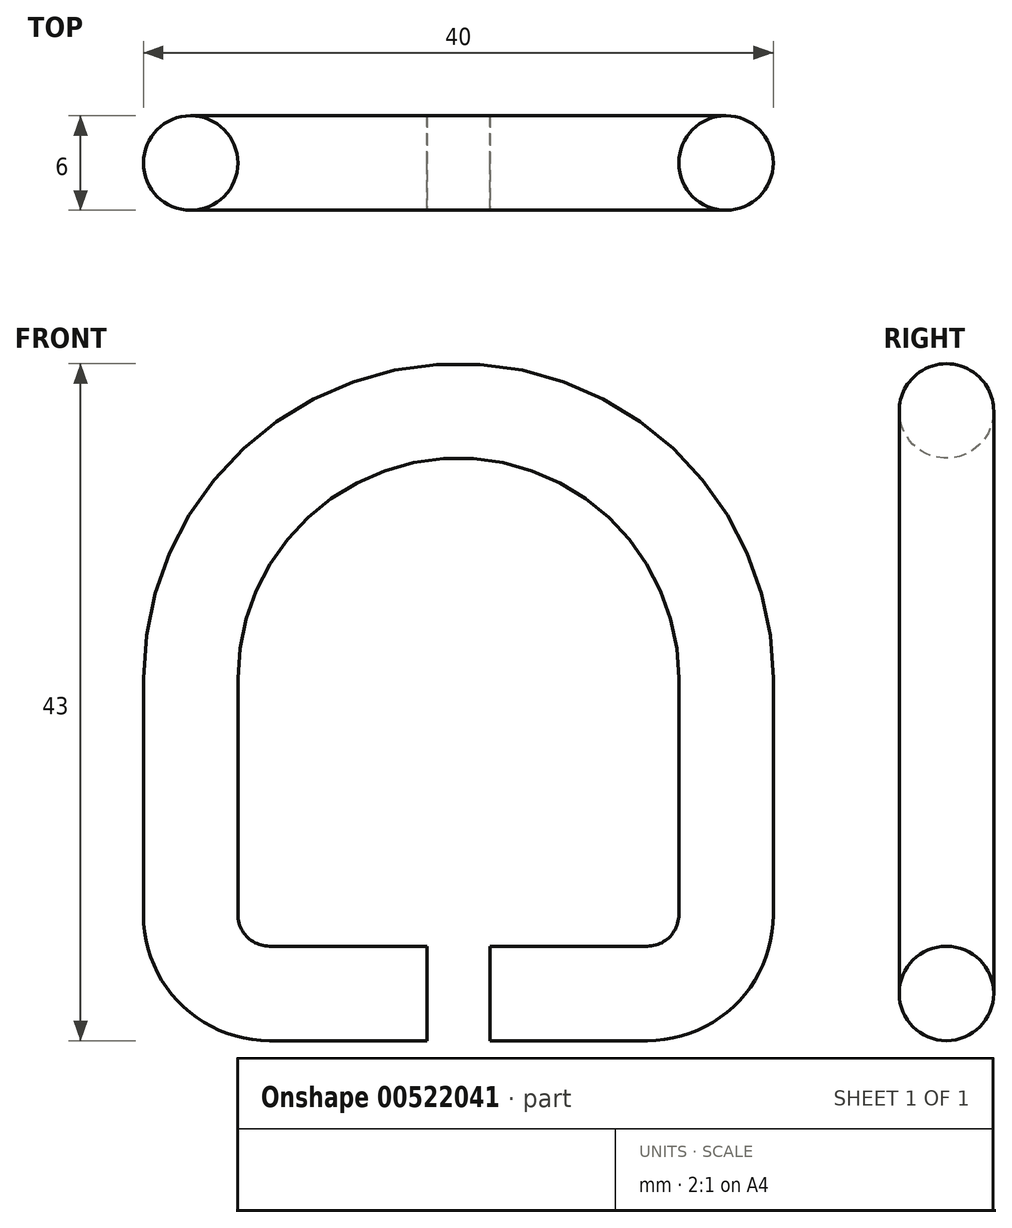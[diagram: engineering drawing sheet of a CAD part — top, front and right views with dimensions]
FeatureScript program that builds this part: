
annotation { "Feature Type Name" : "Feature", "Feature Type Description" : "" }
export const myFeature = defineFeature(function(context is Context, id is Id, definition is map)
    precondition{}
    {
        {
            var Q0;
            Q0=qCreatedBy(makeId("Front.planeOp"),FACE);
            var sketch = newSketch(context, id + "F0", { "sketchPlane" : qUnion([Q0])});
            skLineSegment(sketch, "E0", {"start": v(0, 0) * mm, "end": v(10, 0) * mm});
            skLineSegment(sketch, "E1", {"start": v(15, 5) * mm, "end": v(15, 20) * mm});
            skLineSegment(sketch, "E2", {"start": v(-4, 0) * mm, "end": v(-14, 0) * mm});
            skLineSegment(sketch, "E3", {"start": v(-19, 5) * mm, "end": v(-19, 20) * mm});
            skArc(sketch, "E4", {"start": v(15, 20) * mm, "mid": v(-2, 37) * mm, "end": v(-19, 20) * mm});
            skArc(sketch, "E5", {"start": v(-19, 5) * mm, "mid": v(-17.54, 1.46) * mm, "end": v(-14, 0) * mm});
            skArc(sketch, "E6", {"start": v(10, 0) * mm, "mid": v(13.54, 1.46) * mm, "end": v(15, 5) * mm});
            skSolve(sketch);
        }
        {
            var Q0;
            Q0=qCreatedBy(makeId("Right.planeOp"),FACE);
            var sketch = newSketch(context, id + "F1", { "sketchPlane" : qUnion([Q0])});
            skCircle(sketch, "E7", {"center": v(0, 0) * mm, "radius": 3 * mm});
            skSolve(sketch);
        }
        {
            var Q0;
            Q0=makeQuery(id+"F1.imprint","IMPRINT",FACE,{"disambiguationData":[TD([[makeQuery(id+"F1.imprint","IMPRINT",EDGE,{"derivedFrom":sQuery(id+"F1.wireOp",EDGE,"E7")}),1.0]])]});
            var Q1;
            Q1=sQuery(id+"F0.wireOp",EDGE,"E0");
            var Q2;
            Q2=sQuery(id+"F0.wireOp",EDGE,"E6");
            var Q3;
            Q3=sQuery(id+"F0.wireOp",EDGE,"E1");
            var Q4;
            Q4=sQuery(id+"F0.wireOp",EDGE,"E4");
            var Q5;
            Q5=sQuery(id+"F0.wireOp",EDGE,"E3");
            var Q6;
            Q6=sQuery(id+"F0.wireOp",EDGE,"E5");
            var Q7;
            Q7=sQuery(id+"F0.wireOp",EDGE,"E2");
            sweep(context, id + "F2", {"profiles" : qUnion([Q0]), "path" : qUnion([Q1, Q2, Q3, Q4, Q5, Q6, Q7])});
        }
    });
